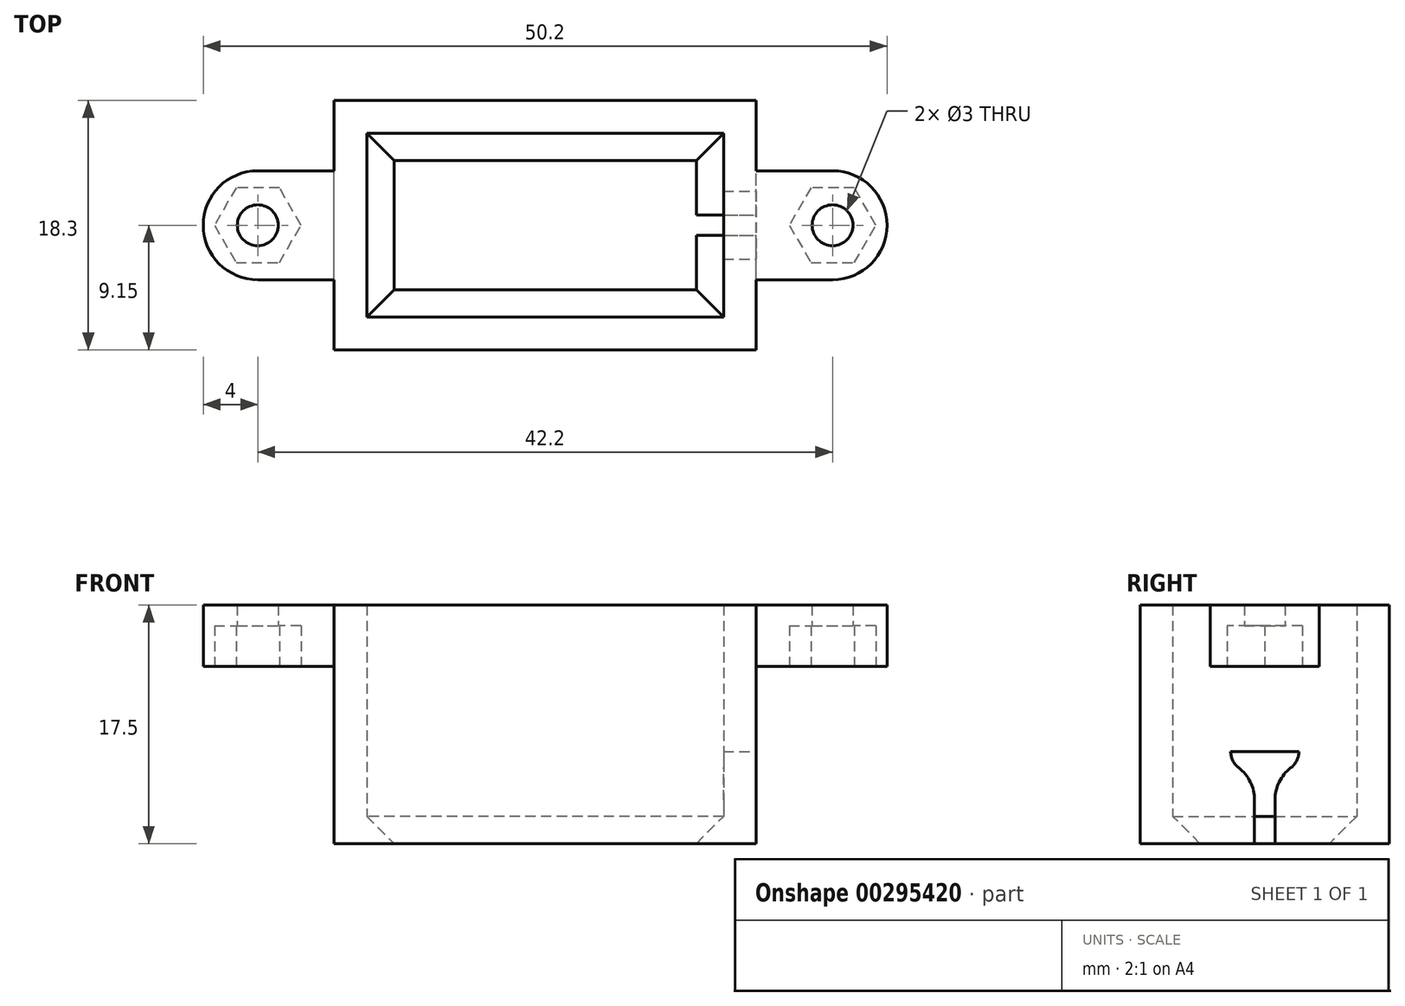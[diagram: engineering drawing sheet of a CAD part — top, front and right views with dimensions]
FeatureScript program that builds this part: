
annotation { "Feature Type Name" : "Feature", "Feature Type Description" : "" }
export const myFeature = defineFeature(function(context is Context, id is Id, definition is map)
    precondition{}
    {
        {
            var Q0;
            Q0=qCreatedBy(makeId("Top.planeOp"),FACE);
            var sketch = newSketch(context, id + "F0", { "sketchPlane" : qUnion([Q0])});
            skLineSegment(sketch, "E0.bottom", {"start": v(13.1, -6.75) * mm, "end": v(-13.1, -6.75) * mm});
            skLineSegment(sketch, "E0.top", {"start": v(13.1, 6.75) * mm, "end": v(-13.1, 6.75) * mm});
            skLineSegment(sketch, "E0.left", {"start": v(13.1, -6.75) * mm, "end": v(13.1, 6.75) * mm});
            skLineSegment(sketch, "E0.right", {"start": v(-13.1, -6.75) * mm, "end": v(-13.1, 6.75) * mm});
            skPoint(sketch, "E0.middle", {"position": v(0, 0) * mm});
            skLineSegment(sketch, "E1.bottom", {"start": v(15.5, -9.15) * mm, "end": v(-15.5, -9.15) * mm});
            skLineSegment(sketch, "E1.top", {"start": v(15.5, 9.15) * mm, "end": v(-15.5, 9.15) * mm});
            skLineSegment(sketch, "E1.left", {"start": v(15.5, -9.15) * mm, "end": v(15.5, 9.15) * mm});
            skLineSegment(sketch, "E1.right", {"start": v(-15.5, -9.15) * mm, "end": v(-15.5, 9.15) * mm});
            skSolve(sketch);
        }
        {
            var Q0;
            Q0 = qSketchRegion(id + "F0", true);
            extrude(context, id + "F1", {"entities" : qUnion([Q0]), "depth" : 17.5 * mm});
        }
        {
            var Q0;
            Q0=makeQuery(id+"F1.opExtrude","CAP_FACE",FACE,{"disambiguationData":[OSD([sQuery(id+"F0.wireOp",EDGE,"E0.bottom"),sQuery(id+"F0.wireOp",EDGE,"E0.top"),sQuery(id+"F0.wireOp",EDGE,"E0.left"),sQuery(id+"F0.wireOp",EDGE,"E0.right"),sQuery(id+"F0.wireOp",EDGE,"E1.bottom"),sQuery(id+"F0.wireOp",EDGE,"E1.top"),sQuery(id+"F0.wireOp",EDGE,"E1.left"),sQuery(id+"F0.wireOp",EDGE,"E1.right")])],"isStart":true});
            var sketch = newSketch(context, id + "F2", { "sketchPlane" : qUnion([Q0])});
            skLineSegment(sketch, "E2.0", {"start": v(13.1, 6.75) * mm, "end": v(-13.1, 6.75) * mm});
            skLineSegment(sketch, "E3.0", {"start": v(-13.1, 6.75) * mm, "end": v(-13.1, -6.75) * mm});
            skLineSegment(sketch, "E4.0", {"start": v(13.1, -6.75) * mm, "end": v(-13.1, -6.75) * mm});
            skLineSegment(sketch, "E5.0", {"start": v(13.1, 6.75) * mm, "end": v(13.1, -6.75) * mm});
            skLineSegment(sketch, "E6.bottom", {"start": v(11.1, -4.75) * mm, "end": v(-11.1, -4.75) * mm});
            skLineSegment(sketch, "E6.top", {"start": v(11.1, 4.75) * mm, "end": v(-11.1, 4.75) * mm});
            skLineSegment(sketch, "E6.left", {"start": v(11.1, -4.75) * mm, "end": v(11.1, 4.75) * mm});
            skLineSegment(sketch, "E6.right", {"start": v(-11.1, -4.75) * mm, "end": v(-11.1, 4.75) * mm});
            skPoint(sketch, "E6.middle", {"position": v(0, 0) * mm});
            skSolve(sketch);
        }
        {
            var Q0;
            Q0 = qSketchRegion(id + "F2", true);
            extrude(context, id + "F3", {"entities" : qUnion([Q0]), "operationType" : NewBodyOperationType.ADD, "oppositeDirection" : true, "depth" : 2 * mm});
        }
        {
            var Q0;
            Q0=makeQuery(id+"F3.opExtrude","CAP_EDGE",EDGE,{"disambiguationData":[OSD([sQuery(id+"F2.wireOp",EDGE,"E6.bottom")])],"isStart":false});
            var Q1;
            Q1=makeQuery(id+"F3.opExtrude","CAP_EDGE",EDGE,{"disambiguationData":[OSD([sQuery(id+"F2.wireOp",EDGE,"E6.left")])],"isStart":false});
            var Q2;
            Q2=makeQuery(id+"F3.opExtrude","CAP_EDGE",EDGE,{"disambiguationData":[OSD([sQuery(id+"F2.wireOp",EDGE,"E6.top")])],"isStart":false});
            var Q3;
            Q3=makeQuery(id+"F3.opExtrude","CAP_EDGE",EDGE,{"disambiguationData":[OSD([sQuery(id+"F2.wireOp",EDGE,"E6.right")])],"isStart":false});
            chamfer(context, id + "F4", {"entities" : qUnion([Q0, Q1, Q2, Q3]), "width" : 2 * mm, "tangentPropagation" : true});
        }
        {
            var Q0;
            Q0=qCreatedBy(makeId("Top.planeOp"),FACE);
            var sketch = newSketch(context, id + "F5", { "sketchPlane" : qUnion([Q0])});
            skArc(sketch, "E7", {"start": v(21.1, -4) * mm, "mid": v(25.1, 0) * mm, "end": v(21.1, 4) * mm});
            skLineSegment(sketch, "E8.0", {"start": v(15.5, -4) * mm, "end": v(15.5, 4) * mm});
            skLineSegment(sketch, "E9.0", {"start": v(17.1, -9.15) * mm, "end": v(17.1, 9.15) * mm, "construction": true});
            skLineSegment(sketch, "E10", {"start": v(17.1, 4) * mm, "end": v(21.1, 4) * mm});
            skLineSegment(sketch, "E11.MirrorCS", {"start": v(17.1, -4) * mm, "end": v(21.1, -4) * mm});
            skLineSegment(sketch, "E12", {"start": v(17.1, 4) * mm, "end": v(15.5, 4) * mm});
            skLineSegment(sketch, "E13", {"start": v(17.1, -4) * mm, "end": v(15.5, -4) * mm});
            skPoint(sketch, "E14.orphan", {"position": v(33.8, -4) * mm});
            skPoint(sketch, "E15.orphan", {"position": v(33.8, 4) * mm});
            skCircle(sketch, "E16", {"center": v(21.1, 0) * mm, "radius": 1.5 * mm});
            skPoint(sketch, "E17.orphan", {"position": v(15.5, -9.15) * mm});
            skPoint(sketch, "E18.orphan", {"position": v(15.5, 9.15) * mm});
            skArc(sketch, "E19.MirrorCS", {"start": v(-21.1, -4) * mm, "mid": v(-25.1, 0) * mm, "end": v(-21.1, 4) * mm});
            skPoint(sketch, "E20.MirrorP", {"position": v(-33.8, -4) * mm});
            skPoint(sketch, "E21.MirrorP", {"position": v(-33.8, 4) * mm});
            skLineSegment(sketch, "E22.MirrorCS", {"start": v(-17.1, -4) * mm, "end": v(-21.1, -4) * mm});
            skLineSegment(sketch, "E23.MirrorCS", {"start": v(-17.1, 4) * mm, "end": v(-21.1, 4) * mm});
            skCircle(sketch, "E24.MirrorC", {"center": v(-21.1, 0) * mm, "radius": 1.5 * mm});
            skLineSegment(sketch, "E25.MirrorCS", {"start": v(-15.5, -4) * mm, "end": v(-15.5, 4) * mm});
            skLineSegment(sketch, "E26.MirrorCS", {"start": v(-17.1, 4) * mm, "end": v(-15.5, 4) * mm});
            skLineSegment(sketch, "E27.MirrorCS", {"start": v(-17.1, -4) * mm, "end": v(-15.5, -4) * mm});
            skSolve(sketch);
        }
        {
            var Q0;
            Q0 = qSketchRegion(id + "F5", true);
            var Q1;
            Q1=makeQuery(id+"F1.opExtrude","CAP_FACE",FACE,{"disambiguationData":[OSD([sQuery(id+"F0.wireOp",EDGE,"E0.bottom"),sQuery(id+"F0.wireOp",EDGE,"E0.top"),sQuery(id+"F0.wireOp",EDGE,"E0.left"),sQuery(id+"F0.wireOp",EDGE,"E0.right"),sQuery(id+"F0.wireOp",EDGE,"E1.bottom"),sQuery(id+"F0.wireOp",EDGE,"E1.top"),sQuery(id+"F0.wireOp",EDGE,"E1.left"),sQuery(id+"F0.wireOp",EDGE,"E1.right")])],"isStart":false});
            extrude(context, id + "F6", {"entities" : qUnion([Q0]), "operationType" : NewBodyOperationType.ADD, "endBound" : BoundingType.UP_TO_SURFACE, "endBoundEntityFace" : qUnion([Q1]), "depth" : 20 * mm, "hasSecondDirection" : true, "secondDirectionOppositeDirection" : false, "secondDirectionDepth" : 13 * mm});
        }
        {
            var Q0;
            Q0=makeQuery(id+"F6.opExtrude","CAP_FACE",FACE,{"disambiguationData":[OSD([sQuery(id+"F5.wireOp",EDGE,"E19.MirrorCS"),sQuery(id+"F5.wireOp",EDGE,"E22.MirrorCS"),sQuery(id+"F5.wireOp",EDGE,"E23.MirrorCS"),sQuery(id+"F5.wireOp",EDGE,"E24.MirrorC"),sQuery(id+"F5.wireOp",EDGE,"E25.MirrorCS"),sQuery(id+"F5.wireOp",EDGE,"E26.MirrorCS"),sQuery(id+"F5.wireOp",EDGE,"E27.MirrorCS")])],"isStart":true});
            var sketch = newSketch(context, id + "F7", { "sketchPlane" : qUnion([Q0])});
            skCircle(sketch, "E28.0", {"center": v(21.1, 0) * mm, "radius": 1.5 * mm, "construction": true});
            skCircle(sketch, "E29.0", {"center": v(-21.1, 0) * mm, "radius": 1.5 * mm, "construction": true});
            skCircle(sketch, "E30.cCircle", {"center": v(21.1, 0) * mm, "radius": 2.75 * mm, "construction": true});
            skLineSegment(sketch, "E30.0", {"start": v(19.51, 2.75) * mm, "end": v(22.69, 2.75) * mm});
            skLineSegment(sketch, "E30.1", {"start": v(22.69, 2.75) * mm, "end": v(24.28, 0) * mm});
            skLineSegment(sketch, "E30.2", {"start": v(24.28, 0) * mm, "end": v(22.69, -2.75) * mm});
            skLineSegment(sketch, "E30.3", {"start": v(22.69, -2.75) * mm, "end": v(19.51, -2.75) * mm});
            skLineSegment(sketch, "E30.4", {"start": v(19.51, -2.75) * mm, "end": v(17.92, 0) * mm});
            skLineSegment(sketch, "E30.5", {"start": v(17.92, 0) * mm, "end": v(19.51, 2.75) * mm});
            skPoint(sketch, "E30.0.midPoint", {"position": v(21.1, 2.75) * mm});
            skCircle(sketch, "E31.cCircle", {"center": v(-21.1, 0) * mm, "radius": 2.75 * mm, "construction": true});
            skLineSegment(sketch, "E31.0", {"start": v(-22.69, 2.75) * mm, "end": v(-19.51, 2.75) * mm});
            skLineSegment(sketch, "E31.1", {"start": v(-19.51, 2.75) * mm, "end": v(-17.92, 0) * mm});
            skLineSegment(sketch, "E31.2", {"start": v(-17.92, 0) * mm, "end": v(-19.51, -2.75) * mm});
            skLineSegment(sketch, "E31.3", {"start": v(-19.51, -2.75) * mm, "end": v(-22.69, -2.75) * mm});
            skLineSegment(sketch, "E31.4", {"start": v(-22.69, -2.75) * mm, "end": v(-24.28, 0) * mm});
            skLineSegment(sketch, "E31.5", {"start": v(-24.28, 0) * mm, "end": v(-22.69, 2.75) * mm});
            skPoint(sketch, "E31.0.midPoint", {"position": v(-21.1, 2.75) * mm});
            skSolve(sketch);
        }
        {
            var Q0;
            Q0 = qSketchRegion(id + "F7", true);
            extrude(context, id + "F8", {"entities" : qUnion([Q0]), "operationType" : NewBodyOperationType.REMOVE, "oppositeDirection" : true, "depth" : 3 * mm});
        }
        {
            var Q0;
            Q0=makeQuery(id+"F1.opExtrude","SWEPT_FACE",FACE,{"disambiguationData":[OSD([sQuery(id+"F0.wireOp",EDGE,"E1.left")])]});
            var sketch = newSketch(context, id + "F9", { "sketchPlane" : qUnion([Q0])});
            skLineSegment(sketch, "E32", {"start": v(0, 0) * mm, "end": v(0, 6) * mm, "construction": true});
            skLineSegment(sketch, "E33.bottom", {"start": v(2.5, 5.25) * mm, "end": v(0.75, 5.25) * mm});
            skLineSegment(sketch, "E33.top", {"start": v(2.5, 6.75) * mm, "end": v(-2.5, 6.75) * mm});
            skLineSegment(sketch, "E33.left", {"start": v(2.5, 5.25) * mm, "end": v(2.5, 6.75) * mm});
            skLineSegment(sketch, "E33.right", {"start": v(-2.5, 5.25) * mm, "end": v(-2.5, 6.75) * mm});
            skPoint(sketch, "E33.middle", {"position": v(0, 6) * mm});
            skLineSegment(sketch, "E34", {"start": v(0.75, 0) * mm, "end": v(0.75, 5.25) * mm});
            skLineSegment(sketch, "E35", {"start": v(-0.75, 0) * mm, "end": v(-0.75, 5.25) * mm});
            skLineSegment(sketch, "E36", {"start": v(0.75, 0) * mm, "end": v(-0.75, 0) * mm});
            skLineSegment(sketch, "E37.trimOffspring", {"start": v(-0.75, 5.25) * mm, "end": v(-2.5, 5.25) * mm});
            skSolve(sketch);
        }
        {
            var Q0;
            Q0 = qSketchRegion(id + "F9", true);
            extrude(context, id + "F10", {"entities" : qUnion([Q0]), "operationType" : NewBodyOperationType.REMOVE, "oppositeDirection" : true, "depth" : 5 * mm});
        }
        {
            var Q0;
            Q0=makeQuery(id+"F10.boolean.opBoolean","COPY",EDGE,{"derivedFrom":makeQuery(id+"F10.opExtrude","SWEPT_EDGE",EDGE,{"disambiguationData":[OSD([sQuery(id+"F9.wireOp",EDGE,"E33.right"),sQuery(id+"F9.wireOp",EDGE,"E37.trimOffspring")])]})});
            var Q1;
            Q1=makeQuery(id+"F10.boolean.opBoolean","COPY",EDGE,{"derivedFrom":makeQuery(id+"F10.opExtrude","SWEPT_EDGE",EDGE,{"disambiguationData":[OSD([sQuery(id+"F9.wireOp",EDGE,"E33.bottom"),sQuery(id+"F9.wireOp",EDGE,"E33.left")])]})});
            fillet(context, id + "F11", {"entities" : qUnion([Q0, Q1]), "radius" : 1.5 * mm, "tangentPropagation" : true, "allowEdgeOverflow" : false});
        }
        {
            var Q0;
            Q0=makeQuery(id+"F10.boolean.opBoolean","COPY",EDGE,{"derivedFrom":makeQuery(id+"F10.opExtrude","SWEPT_EDGE",EDGE,{"disambiguationData":[OSD([sQuery(id+"F9.wireOp",EDGE,"E35"),sQuery(id+"F9.wireOp",EDGE,"E37.trimOffspring")])]})});
            var Q1;
            Q1=makeQuery(id+"F10.boolean.opBoolean","COPY",EDGE,{"derivedFrom":makeQuery(id+"F10.opExtrude","SWEPT_EDGE",EDGE,{"disambiguationData":[OSD([sQuery(id+"F9.wireOp",EDGE,"E33.bottom"),sQuery(id+"F9.wireOp",EDGE,"E34")])]})});
            fillet(context, id + "F12", {"entities" : qUnion([Q0, Q1]), "radius" : 3 * mm, "tangentPropagation" : true, "allowEdgeOverflow" : false});
        }
    });
